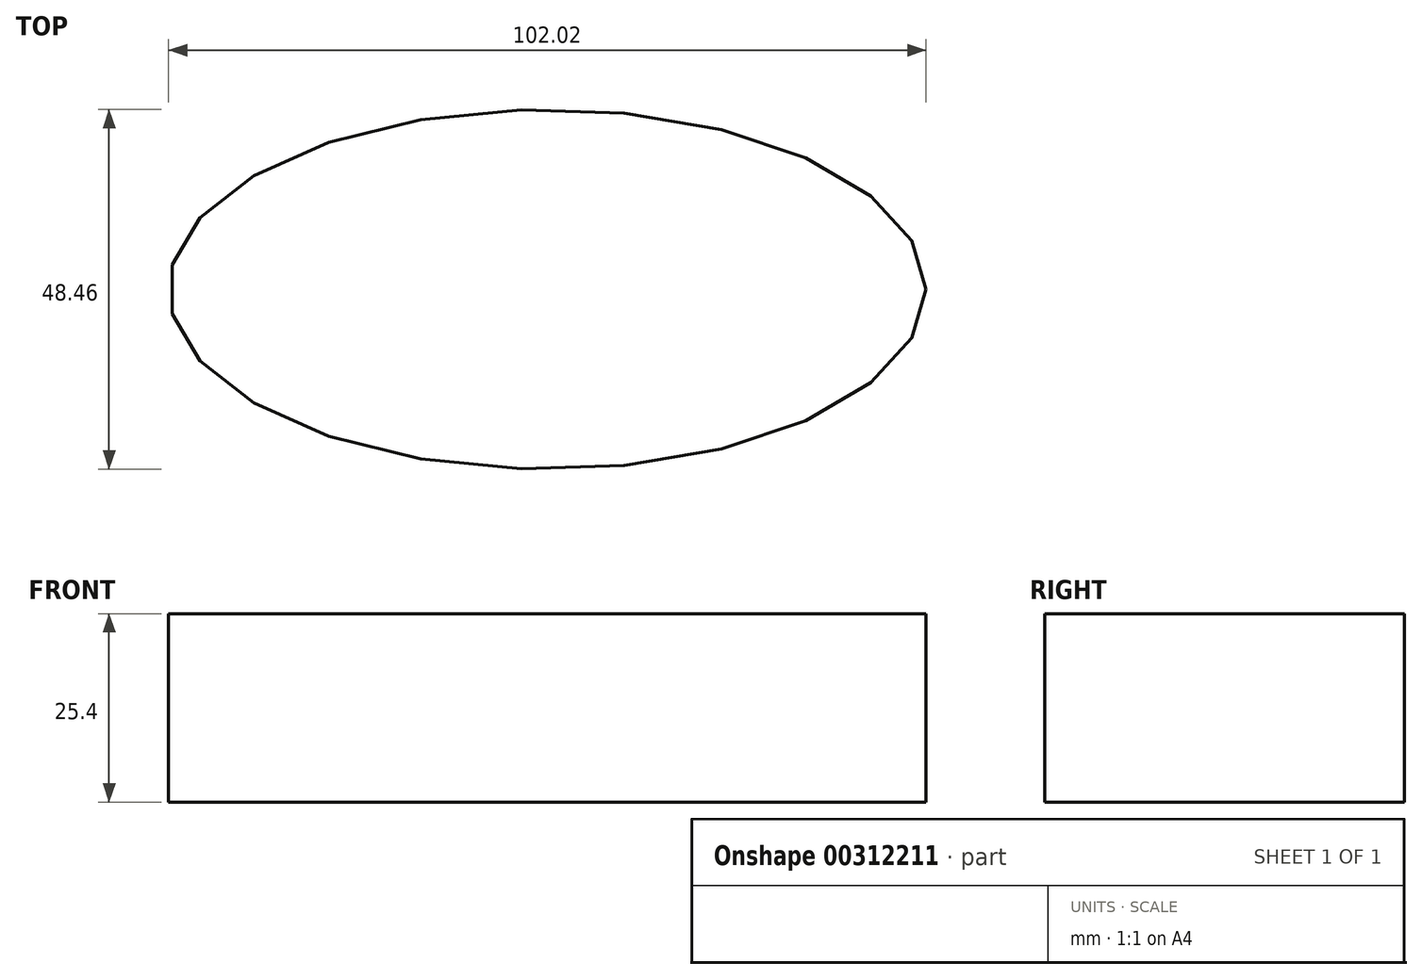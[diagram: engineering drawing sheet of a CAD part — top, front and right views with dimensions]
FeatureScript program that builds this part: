
annotation { "Feature Type Name" : "Feature", "Feature Type Description" : "" }
export const myFeature = defineFeature(function(context is Context, id is Id, definition is map)
    precondition{}
    {
        {
            var Q0;
            Q0=qCreatedBy(makeId("Top.planeOp"),FACE);
            var sketch = newSketch(context, id + "F0", { "sketchPlane" : qUnion([Q0])});
            skEllipse(sketch, "E0", {"center": v(0, 0) * mm, "majorRadius": 51.01 * mm, "minorRadius": 24.23 * mm, "majorAxis": v(1, 0)});
            skSolve(sketch);
        }
        {
            var Q0;
            Q0 = qSketchRegion(id + "F0", true);
            extrude(context, id + "F1", {"entities" : qUnion([Q0]), "depth" : 25.4 * mm});
        }
    });
